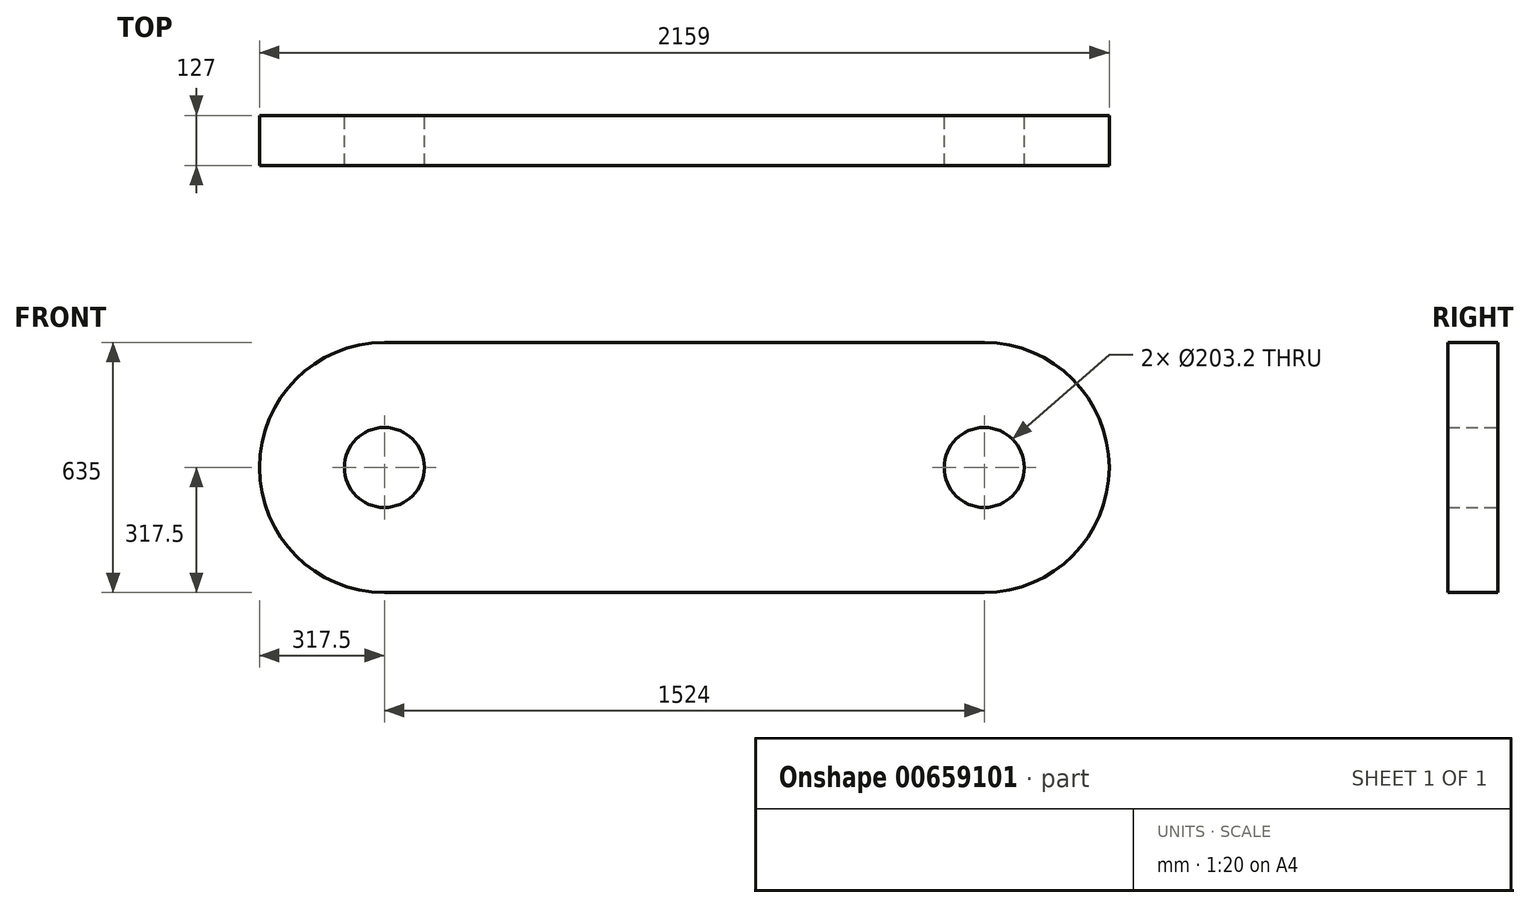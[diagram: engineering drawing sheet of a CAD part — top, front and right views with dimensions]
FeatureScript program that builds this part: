
annotation { "Feature Type Name" : "Feature", "Feature Type Description" : "" }
export const myFeature = defineFeature(function(context is Context, id is Id, definition is map)
    precondition{}
    {
        {
            var Q0;
            Q0=qCreatedBy(makeId("Front.planeOp"),FACE);
            var sketch = newSketch(context, id + "F0", { "sketchPlane" : qUnion([Q0])});
            skArc(sketch, "E0", {"start": v(-762, 317.5) * mm, "mid": v(-1079.5, 0) * mm, "end": v(-762, -317.5) * mm});
            skLineSegment(sketch, "E1", {"start": v(-762, 317.5) * mm, "end": v(0, 317.5) * mm});
            skLineSegment(sketch, "E2", {"start": v(-762, -317.5) * mm, "end": v(0, -317.5) * mm});
            skCircle(sketch, "E3", {"center": v(-762, 0) * mm, "radius": 101.6 * mm});
            skLineSegment(sketch, "E4.MirrorCS", {"start": v(762, 317.5) * mm, "end": v(0, 317.5) * mm});
            skArc(sketch, "E5.MirrorCS", {"start": v(762, 317.5) * mm, "mid": v(1079.5, 0) * mm, "end": v(762, -317.5) * mm});
            skCircle(sketch, "E6.MirrorC", {"center": v(762, 0) * mm, "radius": 101.6 * mm});
            skLineSegment(sketch, "E7.MirrorCS", {"start": v(762, -317.5) * mm, "end": v(0, -317.5) * mm});
            skSolve(sketch);
        }
        {
            var Q0;
            Q0 = qSketchRegion(id + "F0", true);
            extrude(context, id + "F1", {"entities" : qUnion([Q0]), "depth" : 127 * mm, "offsetDistance" : 25.4 * mm});
        }
    });
